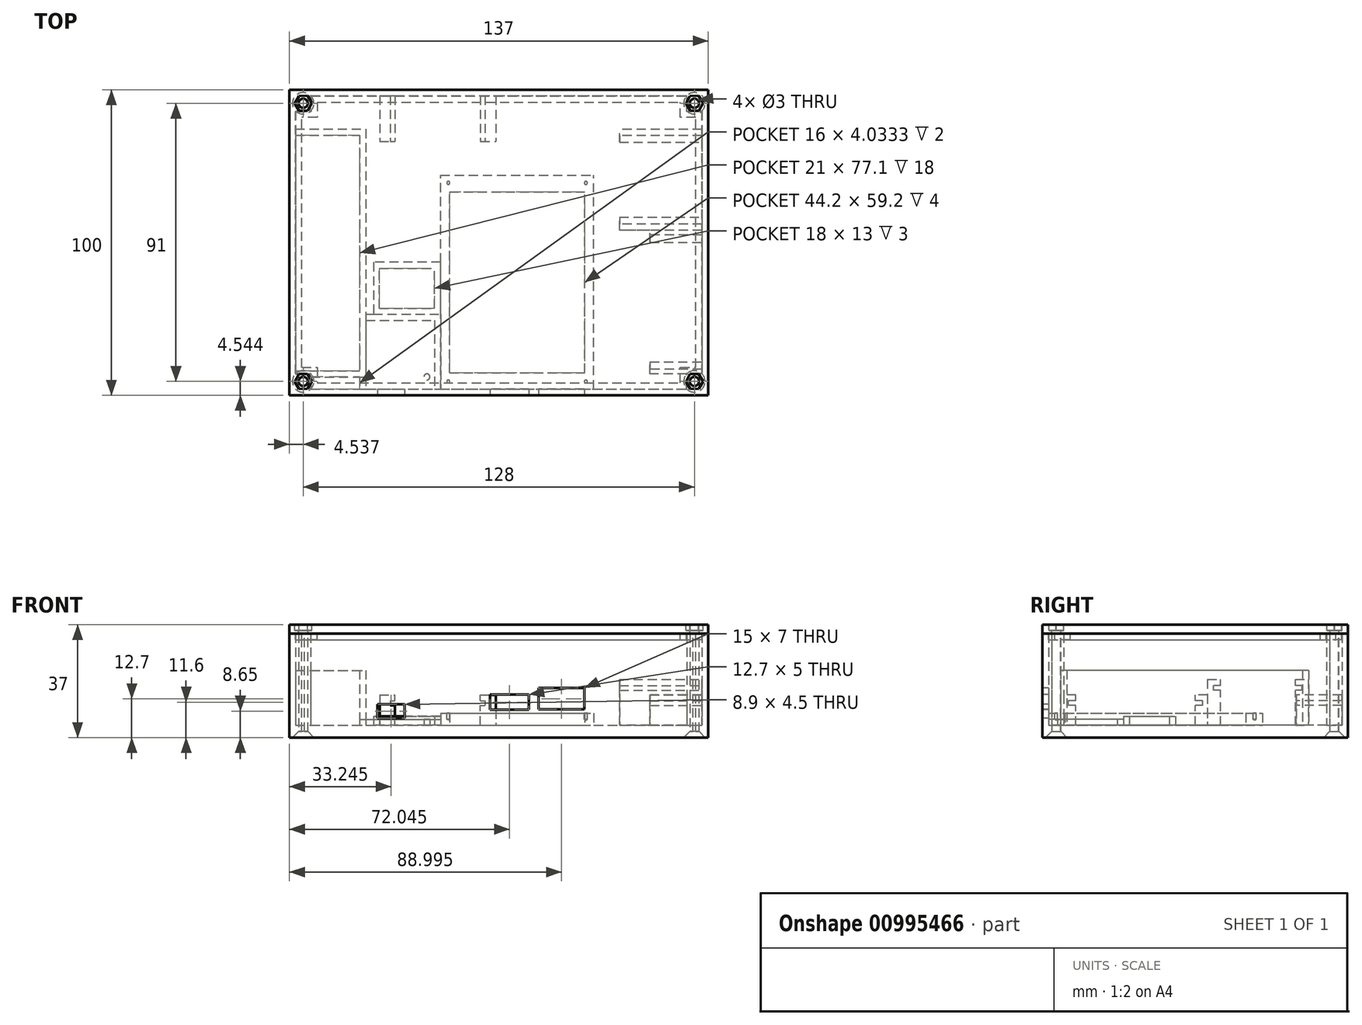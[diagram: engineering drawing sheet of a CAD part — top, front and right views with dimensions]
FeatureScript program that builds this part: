
annotation { "Feature Type Name" : "Feature", "Feature Type Description" : "" }
export const myFeature = defineFeature(function(context is Context, id is Id, definition is map)
    precondition{}
    {
        {
            var Q0;
            Q0=qCreatedBy(makeId("Top.planeOp"),FACE);
            var sketch = newSketch(context, id + "F0", { "sketchPlane" : qUnion([Q0])});
            skLineSegment(sketch, "E0.bottom", {"start": v(-82.47, 29.01) * mm, "end": v(54.53, 29.01) * mm});
            skLineSegment(sketch, "E0.top", {"start": v(-82.47, -70.99) * mm, "end": v(54.53, -70.99) * mm});
            skLineSegment(sketch, "E0.left", {"start": v(-82.47, 29.01) * mm, "end": v(-82.47, -70.99) * mm});
            skLineSegment(sketch, "E0.right", {"start": v(54.53, 29.01) * mm, "end": v(54.53, -70.99) * mm});
            skSolve(sketch);
        }
        {
            var Q0;
            Q0=makeQuery(id+"F0.imprint","IMPRINT",FACE,{"disambiguationData":[TD([[makeQuery(id+"F0.imprint","IMPRINT",EDGE,{"derivedFrom":sQuery(id+"F0.wireOp",EDGE,"E0.bottom")}),-1.0]])]});
            extrude(context, id + "F1", {"entities" : qUnion([Q0]), "oppositeDirection" : true, "depth" : 4 * mm, "offsetDistance" : 25 * mm});
        }
        {
            var Q0;
            Q0=makeQuery(id+"F1.opExtrude","CAP_FACE",FACE,{"disambiguationData":[OSD([sQuery(id+"F0.wireOp",EDGE,"E0.bottom"),sQuery(id+"F0.wireOp",EDGE,"E0.top"),sQuery(id+"F0.wireOp",EDGE,"E0.left"),sQuery(id+"F0.wireOp",EDGE,"E0.right")])],"isStart":true});
            var sketch = newSketch(context, id + "F2", { "sketchPlane" : qUnion([Q0])});
            skLineSegment(sketch, "E1.bottom", {"start": v(-80.47, 27.01) * mm, "end": v(52.53, 27.01) * mm});
            skLineSegment(sketch, "E1.top", {"start": v(-80.47, -68.99) * mm, "end": v(52.53, -68.99) * mm});
            skLineSegment(sketch, "E1.left", {"start": v(-80.47, 27.01) * mm, "end": v(-80.47, -68.99) * mm});
            skLineSegment(sketch, "E1.right", {"start": v(52.53, 27.01) * mm, "end": v(52.53, -68.99) * mm});
            skSolve(sketch);
        }
        {
            var Q0;
            Q0=makeQuery(id+"F2.imprint","IMPRINT",FACE,{"disambiguationData":[TD([[makeQuery(id+"F2.imprint","IMPRINT",EDGE,{"derivedFrom":sQuery(id+"F2.wireOp",EDGE,"E1.bottom")}),1.0]])]});
            extrude(context, id + "F3", {"entities" : qUnion([Q0]), "operationType" : NewBodyOperationType.ADD, "depth" : 30 * mm, "offsetDistance" : 25 * mm});
        }
        {
            var Q0;
            Q0=makeQuery(id+"F1.opExtrude","CAP_FACE",FACE,{"disambiguationData":[OSD([sQuery(id+"F0.wireOp",EDGE,"E0.bottom"),sQuery(id+"F0.wireOp",EDGE,"E0.top"),sQuery(id+"F0.wireOp",EDGE,"E0.left"),sQuery(id+"F0.wireOp",EDGE,"E0.right")])],"isStart":true});
            var sketch = newSketch(context, id + "F4", { "sketchPlane" : qUnion([Q0])});
            skLineSegment(sketch, "E2.bottom", {"start": v(-80.47, 22.01) * mm, "end": v(-75.47, 22.01) * mm});
            skLineSegment(sketch, "E2.top", {"start": v(-80.47, 27.01) * mm, "end": v(-75.47, 27.01) * mm});
            skLineSegment(sketch, "E2.left", {"start": v(-80.47, 22.01) * mm, "end": v(-80.47, 27.01) * mm});
            skLineSegment(sketch, "E2.right", {"start": v(-75.47, 22.01) * mm, "end": v(-75.47, 27.01) * mm});
            skLineSegment(sketch, "E3.0.1.0", {"start": v(-80.47, -68.99) * mm, "end": v(-75.47, -68.99) * mm});
            skLineSegment(sketch, "E3.0.1.1", {"start": v(-75.47, -68.99) * mm, "end": v(-75.47, -63.99) * mm});
            skLineSegment(sketch, "E3.0.1.2", {"start": v(-80.47, -63.99) * mm, "end": v(-75.47, -63.99) * mm});
            skLineSegment(sketch, "E3.0.1.3", {"start": v(-80.47, -68.99) * mm, "end": v(-80.47, -63.99) * mm});
            skLineSegment(sketch, "E3.1.0.0", {"start": v(47.53, 22.01) * mm, "end": v(52.53, 22.01) * mm});
            skLineSegment(sketch, "E3.1.0.1", {"start": v(52.53, 22.01) * mm, "end": v(52.53, 27.01) * mm});
            skLineSegment(sketch, "E3.1.0.2", {"start": v(47.53, 27.01) * mm, "end": v(52.53, 27.01) * mm});
            skLineSegment(sketch, "E3.1.0.3", {"start": v(47.53, 22.01) * mm, "end": v(47.53, 27.01) * mm});
            skLineSegment(sketch, "E3.1.1.0", {"start": v(47.53, -68.99) * mm, "end": v(52.53, -68.99) * mm});
            skLineSegment(sketch, "E3.1.1.1", {"start": v(52.53, -68.99) * mm, "end": v(52.53, -63.99) * mm});
            skLineSegment(sketch, "E3.1.1.2", {"start": v(47.53, -63.99) * mm, "end": v(52.53, -63.99) * mm});
            skLineSegment(sketch, "E3.1.1.3", {"start": v(47.53, -68.99) * mm, "end": v(47.53, -63.99) * mm});
            skLineSegment(sketch, "E3.direction1", {"start": v(-80.47, 22.01) * mm, "end": v(47.53, 22.01) * mm, "construction": true});
            skLineSegment(sketch, "E3.direction2", {"start": v(-80.47, 22.01) * mm, "end": v(-80.47, -68.99) * mm, "construction": true});
            skSolve(sketch);
        }
        {
            var Q0;
            Q0=makeQuery(id+"F4.imprint","IMPRINT",FACE,{"disambiguationData":[TD([[makeQuery(id+"F4.imprint","IMPRINT",EDGE,{"derivedFrom":sQuery(id+"F4.wireOp",EDGE,"E2.bottom")}),1.0]])]});
            var Q1;
            Q1=makeQuery(id+"F4.imprint","IMPRINT",FACE,{"disambiguationData":[TD([[makeQuery(id+"F4.imprint","IMPRINT",EDGE,{"derivedFrom":sQuery(id+"F4.wireOp",EDGE,"E3.1.0.0")}),1.0]])]});
            var Q2;
            Q2=makeQuery(id+"F4.imprint","IMPRINT",FACE,{"disambiguationData":[TD([[makeQuery(id+"F4.imprint","IMPRINT",EDGE,{"derivedFrom":sQuery(id+"F4.wireOp",EDGE,"E3.1.1.0")}),1.0]])]});
            var Q3;
            Q3=makeQuery(id+"F4.imprint","IMPRINT",FACE,{"disambiguationData":[TD([[makeQuery(id+"F4.imprint","IMPRINT",EDGE,{"derivedFrom":sQuery(id+"F4.wireOp",EDGE,"E3.0.1.0")}),1.0]])]});
            extrude(context, id + "F5", {"entities" : qUnion([Q0, Q1, Q2, Q3]), "operationType" : NewBodyOperationType.ADD, "depth" : 30 * mm, "offsetDistance" : 25 * mm});
        }
        {
            var Q0;
            Q0=makeQuery(id+"F1.opExtrude","CAP_FACE",FACE,{"disambiguationData":[OSD([sQuery(id+"F0.wireOp",EDGE,"E0.bottom"),sQuery(id+"F0.wireOp",EDGE,"E0.top"),sQuery(id+"F0.wireOp",EDGE,"E0.left"),sQuery(id+"F0.wireOp",EDGE,"E0.right")])],"isStart":false});
            var sketch = newSketch(context, id + "F6", { "sketchPlane" : qUnion([Q0])});
            skCircle(sketch, "E4", {"center": v(-77.96, 66.46) * mm, "radius": 1.5 * mm});
            skCircle(sketch, "E5.0.1.0", {"center": v(-77.96, -24.54) * mm, "radius": 1.5 * mm});
            skCircle(sketch, "E5.1.0.0", {"center": v(50.04, 66.46) * mm, "radius": 1.5 * mm});
            skCircle(sketch, "E5.1.1.0", {"center": v(50.04, -24.54) * mm, "radius": 1.5 * mm});
            skLineSegment(sketch, "E5.direction1", {"start": v(-77.96, 66.46) * mm, "end": v(50.04, 66.46) * mm, "construction": true});
            skLineSegment(sketch, "E5.direction2", {"start": v(-77.96, 66.46) * mm, "end": v(-77.96, -24.54) * mm, "construction": true});
            skSolve(sketch);
        }
        {
            var Q0;
            Q0=sQuery(id+"F6.wireOp",VERTEX,"E5.direction1.start");
            var Q1;
            Q1=sQuery(id+"F6.wireOp",VERTEX,"E5.direction1.end");
            var Q2;
            Q2=sQuery(id+"F6.wireOp",VERTEX,"E5.1.1.0.center");
            var Q3;
            Q3=sQuery(id+"F6.wireOp",VERTEX,"E5.direction2.end");
            var Q4;
            Q4=makeQuery(id+"F1.opExtrude","SWEPT_BODY",BODY,{"disambiguationData":[OSD([sQuery(id+"F0.wireOp",EDGE,"E0.bottom"),sQuery(id+"F0.wireOp",EDGE,"E0.top"),sQuery(id+"F0.wireOp",EDGE,"E0.left"),sQuery(id+"F0.wireOp",EDGE,"E0.right")])]});
            hole(context, id + "F7", {"style" : HoleStyle.C_SINK, "endStyle" : HoleEndStyle.THROUGH, "holeDiameter" : 3 * mm, "cSinkDiameter" : 7 * mm, "cSinkAngle" : 90 * degree, "majorDiameter" : 5 * mm, "isTappedThrough" : true, "tappedDepth" : 12 * mm, "tapClearance" : 3, "startFromSketch" : true, "locations" : qUnion([Q0, Q1, Q2, Q3]), "scope" : qUnion([Q4])});
        }
        {
            var Q0;
            Q0=makeQuery(id+"F1.opExtrude","CAP_FACE",FACE,{"disambiguationData":[OSD([sQuery(id+"F0.wireOp",EDGE,"E0.bottom"),sQuery(id+"F0.wireOp",EDGE,"E0.top"),sQuery(id+"F0.wireOp",EDGE,"E0.left"),sQuery(id+"F0.wireOp",EDGE,"E0.right")])],"isStart":true});
            var sketch = newSketch(context, id + "F8", { "sketchPlane" : qUnion([Q0])});
            skLineSegment(sketch, "E6.bottom", {"start": v(-80.47, 16.14) * mm, "end": v(-57.47, 16.14) * mm});
            skLineSegment(sketch, "E6.top", {"start": v(-80.47, -64.96) * mm, "end": v(-57.47, -64.96) * mm});
            skLineSegment(sketch, "E6.left", {"start": v(-80.47, 16.14) * mm, "end": v(-80.47, -64.96) * mm});
            skLineSegment(sketch, "E6.right", {"start": v(-57.47, 16.14) * mm, "end": v(-57.47, -64.96) * mm});
            skLineSegment(sketch, "E7.bottom", {"start": v(-80.47, 14.14) * mm, "end": v(-59.47, 14.14) * mm});
            skLineSegment(sketch, "E7.top", {"start": v(-80.47, -62.96) * mm, "end": v(-59.47, -62.96) * mm});
            skLineSegment(sketch, "E7.left", {"start": v(-80.47, 14.14) * mm, "end": v(-80.47, -62.96) * mm});
            skLineSegment(sketch, "E7.right", {"start": v(-59.47, 14.14) * mm, "end": v(-59.47, -62.96) * mm});
            skSolve(sketch);
        }
        {
            var Q0;
            {var subQ1=sQuery(id+"F8.wireOp",EDGE,"E6.bottom");Q0=makeQuery(id+"F8.imprint","IMPRINT",FACE,{"disambiguationData":[TD([[makeQuery(id+"F8.imprint","IMPRINT",EDGE,{"derivedFrom":subQ1}),-1.0]])]});}
            extrude(context, id + "F9", {"entities" : qUnion([Q0]), "operationType" : NewBodyOperationType.ADD, "depth" : 18 * mm, "offsetDistance" : 25 * mm});
        }
        {
            var Q0;
            Q0=makeQuery(id+"F9.boolean.opBoolean","SPLIT",FACE,{"disambiguationData":[TD([makeQuery(id+"F3.opExtrude","SWEPT_FACE",FACE,{"disambiguationData":[OSD([sQuery(id+"F2.wireOp",EDGE,"E1.bottom")])]})])],"derivedFrom":makeQuery(id+"F1.opExtrude","CAP_FACE",FACE,{"disambiguationData":[OSD([sQuery(id+"F0.wireOp",EDGE,"E0.bottom"),sQuery(id+"F0.wireOp",EDGE,"E0.top"),sQuery(id+"F0.wireOp",EDGE,"E0.left"),sQuery(id+"F0.wireOp",EDGE,"E0.right")])],"isStart":true})});
            var sketch = newSketch(context, id + "F10", { "sketchPlane" : qUnion([Q0])});
            skLineSegment(sketch, "E8.bottom", {"start": v(-57.47, -46.49) * mm, "end": v(-34.97, -46.49) * mm});
            skLineSegment(sketch, "E8.top", {"start": v(-57.47, -68.99) * mm, "end": v(-34.97, -68.99) * mm});
            skLineSegment(sketch, "E8.left", {"start": v(-57.47, -46.49) * mm, "end": v(-57.47, -68.99) * mm});
            skLineSegment(sketch, "E8.right", {"start": v(-34.97, -46.49) * mm, "end": v(-34.97, -68.99) * mm});
            skLineSegment(sketch, "E9.bottom", {"start": v(-59.47, -44.49) * mm, "end": v(-32.97, -44.49) * mm});
            skLineSegment(sketch, "E9.top", {"start": v(-59.47, -70.99) * mm, "end": v(-32.97, -70.99) * mm});
            skLineSegment(sketch, "E9.left", {"start": v(-59.47, -44.49) * mm, "end": v(-59.47, -70.99) * mm});
            skLineSegment(sketch, "E9.right", {"start": v(-32.97, -44.49) * mm, "end": v(-32.97, -70.99) * mm});
            skCircle(sketch, "E10", {"center": v(-37.47, -64.99) * mm, "radius": 1 * mm});
            skSolve(sketch);
        }
        {
            var Q0;
            {var subQ5=sQuery(id+"F10.wireOp",EDGE,"E8.bottom");Q0=makeQuery(id+"F10.imprint","IMPRINT",FACE,{"disambiguationData":[TD([[makeQuery(id+"F10.imprint","IMPRINT",EDGE,{"derivedFrom":subQ5}),1.0]])]});}
            var Q1;
            Q1=makeQuery(id+"F10.imprint","IMPRINT",FACE,{"disambiguationData":[TD([[makeQuery(id+"F10.imprint","IMPRINT",EDGE,{"derivedFrom":sQuery(id+"F10.wireOp",EDGE,"E10")}),1.0]])]});
            var Q2;
            {var subQ1=makeQuery(id+"F9.opExtrude","CAP_EDGE",EDGE,{"disambiguationData":[OSD([sQuery(id+"F8.wireOp",EDGE,"E6.top")])],"isStart":true});var subQ5=sQuery(id+"F10.wireOp",EDGE,"E9.left");var subQ7=makeQuery(id+"F10.imprint","INTERSECT",VERTEX,{"derivedFrom":[subQ1,subQ5]});Q2=makeQuery(id+"F10.imprint","IMPRINT",FACE,{"disambiguationData":[TD([[makeQuery(id+"F10.imprint","IMPRINT",EDGE,{"disambiguationData":[TD([[subQ7,-1.0]])],"derivedFrom":subQ5}),1.0]])]});}
            extrude(context, id + "F11", {"entities" : qUnion([Q0, Q1, Q2]), "operationType" : NewBodyOperationType.ADD, "depth" : 2 * mm, "offsetDistance" : 25 * mm});
        }
        {
            var Q0;
            {var subQ5=makeQuery(id+"F3.opExtrude","SWEPT_FACE",FACE,{"disambiguationData":[OSD([sQuery(id+"F2.wireOp",EDGE,"E1.bottom")])]});Q0=makeQuery(id+"F11.boolean.opBoolean","SPLIT",FACE,{"disambiguationData":[TD([subQ5])],"derivedFrom":makeQuery(id+"F9.boolean.opBoolean","SPLIT",FACE,{"disambiguationData":[TD([subQ5])],"derivedFrom":makeQuery(id+"F1.opExtrude","CAP_FACE",FACE,{"disambiguationData":[OSD([sQuery(id+"F0.wireOp",EDGE,"E0.bottom"),sQuery(id+"F0.wireOp",EDGE,"E0.top"),sQuery(id+"F0.wireOp",EDGE,"E0.left"),sQuery(id+"F0.wireOp",EDGE,"E0.right")])],"isStart":true})})});}
            var sketch = newSketch(context, id + "F12", { "sketchPlane" : qUnion([Q0])});
            skLineSegment(sketch, "E11.bottom", {"start": v(-32.97, -68.99) * mm, "end": v(17.03, -68.99) * mm});
            skLineSegment(sketch, "E11.top", {"start": v(-32.97, 1.01) * mm, "end": v(17.03, 1.01) * mm});
            skLineSegment(sketch, "E11.left", {"start": v(-32.97, -68.99) * mm, "end": v(-32.97, 1.01) * mm});
            skLineSegment(sketch, "E11.right", {"start": v(17.03, -68.99) * mm, "end": v(17.03, 1.01) * mm});
            skLineSegment(sketch, "E12.bottom", {"start": v(-30.07, -63.59) * mm, "end": v(14.13, -63.59) * mm});
            skLineSegment(sketch, "E12.top", {"start": v(-30.07, -4.39) * mm, "end": v(14.13, -4.39) * mm});
            skLineSegment(sketch, "E12.left", {"start": v(-30.07, -63.59) * mm, "end": v(-30.07, -4.39) * mm});
            skLineSegment(sketch, "E12.right", {"start": v(14.13, -63.59) * mm, "end": v(14.13, -4.39) * mm});
            skSolve(sketch);
        }
        {
            var Q0;
            {var subQ2=sQuery(id+"F12.wireOp",EDGE,"E11.bottom");Q0=makeQuery(id+"F12.imprint","IMPRINT",FACE,{"disambiguationData":[TD([[makeQuery(id+"F12.imprint","IMPRINT",EDGE,{"derivedFrom":subQ2}),1.0]])]});}
            extrude(context, id + "F13", {"entities" : qUnion([Q0]), "operationType" : NewBodyOperationType.ADD, "depth" : 4 * mm, "offsetDistance" : 25 * mm});
        }
        {
            var Q0;
            Q0=makeQuery(id+"F13.opExtrude","CAP_FACE",FACE,{"disambiguationData":[OSD([sQuery(id+"F12.wireOp",EDGE,"E11.bottom"),sQuery(id+"F12.wireOp",EDGE,"E11.top"),sQuery(id+"F12.wireOp",EDGE,"E11.left"),sQuery(id+"F12.wireOp",EDGE,"E11.right"),sQuery(id+"F12.wireOp",EDGE,"E12.bottom"),sQuery(id+"F12.wireOp",EDGE,"E12.top"),sQuery(id+"F12.wireOp",EDGE,"E12.left"),sQuery(id+"F12.wireOp",EDGE,"E12.right")])],"isStart":false});
            var sketch = newSketch(context, id + "F14", { "sketchPlane" : qUnion([Q0])});
            skCircle(sketch, "E13", {"center": v(-30.47, -1.49) * mm, "radius": 1 * mm});
            skCircle(sketch, "E14.0.1.0", {"center": v(-30.47, -66.49) * mm, "radius": 1 * mm});
            skCircle(sketch, "E14.1.0.0", {"center": v(14.53, -1.49) * mm, "radius": 1 * mm});
            skCircle(sketch, "E14.1.1.0", {"center": v(14.53, -66.49) * mm, "radius": 1 * mm});
            skLineSegment(sketch, "E14.direction1", {"start": v(-30.47, -1.49) * mm, "end": v(14.53, -1.49) * mm, "construction": true});
            skLineSegment(sketch, "E14.direction2", {"start": v(-30.47, -1.49) * mm, "end": v(-30.47, -66.49) * mm, "construction": true});
            skSolve(sketch);
        }
        {
            var Q0;
            Q0=sQuery(id+"F14.wireOp",VERTEX,"E14.direction1.start");
            var Q1;
            Q1=sQuery(id+"F14.wireOp",VERTEX,"E14.direction1.end");
            var Q2;
            Q2=sQuery(id+"F14.wireOp",VERTEX,"E14.1.1.0.center");
            var Q3;
            Q3=sQuery(id+"F14.wireOp",VERTEX,"E14.direction2.end");
            var Q4;
            Q4=makeQuery(id+"F1.opExtrude","SWEPT_BODY",BODY,{"disambiguationData":[OSD([sQuery(id+"F0.wireOp",EDGE,"E0.bottom"),sQuery(id+"F0.wireOp",EDGE,"E0.top"),sQuery(id+"F0.wireOp",EDGE,"E0.left"),sQuery(id+"F0.wireOp",EDGE,"E0.right")])]});
            hole(context, id + "F15", {"style" : HoleStyle.SIMPLE, "endStyle" : HoleEndStyle.BLIND, "holeDiameter" : 1 * mm, "majorDiameter" : 5 * mm, "holeDepth" : 2 * mm, "isTappedThrough" : true, "tappedDepth" : 12 * mm, "tapClearance" : 3, "startFromSketch" : true, "locations" : qUnion([Q0, Q1, Q2, Q3]), "scope" : qUnion([Q4])});
        }
        {
            var Q0;
            {var subQ5=makeQuery(id+"F3.opExtrude","SWEPT_FACE",FACE,{"disambiguationData":[OSD([sQuery(id+"F2.wireOp",EDGE,"E1.bottom")])]});Q0=makeQuery(id+"F13.boolean.opBoolean","SPLIT",FACE,{"disambiguationData":[TD([subQ5])],"derivedFrom":makeQuery(id+"F11.boolean.opBoolean","SPLIT",FACE,{"disambiguationData":[TD([subQ5])],"derivedFrom":makeQuery(id+"F9.boolean.opBoolean","SPLIT",FACE,{"disambiguationData":[TD([subQ5])],"derivedFrom":makeQuery(id+"F1.opExtrude","CAP_FACE",FACE,{"disambiguationData":[OSD([sQuery(id+"F0.wireOp",EDGE,"E0.bottom"),sQuery(id+"F0.wireOp",EDGE,"E0.top"),sQuery(id+"F0.wireOp",EDGE,"E0.left"),sQuery(id+"F0.wireOp",EDGE,"E0.right")])],"isStart":true})})})});}
            var sketch = newSketch(context, id + "F16", { "sketchPlane" : qUnion([Q0])});
            skLineSegment(sketch, "E15.bottom", {"start": v(-32.97, -27.49) * mm, "end": v(-54.97, -27.49) * mm});
            skLineSegment(sketch, "E15.top", {"start": v(-32.97, -44.49) * mm, "end": v(-54.97, -44.49) * mm});
            skLineSegment(sketch, "E15.left", {"start": v(-32.97, -27.49) * mm, "end": v(-32.97, -44.49) * mm});
            skLineSegment(sketch, "E15.right", {"start": v(-54.97, -27.49) * mm, "end": v(-54.97, -44.49) * mm});
            skLineSegment(sketch, "E16.bottom", {"start": v(-52.97, -42.49) * mm, "end": v(-34.97, -42.49) * mm});
            skLineSegment(sketch, "E16.top", {"start": v(-52.97, -29.49) * mm, "end": v(-34.97, -29.49) * mm});
            skLineSegment(sketch, "E16.left", {"start": v(-52.97, -42.49) * mm, "end": v(-52.97, -29.49) * mm});
            skLineSegment(sketch, "E16.right", {"start": v(-34.97, -42.49) * mm, "end": v(-34.97, -29.49) * mm});
            skSolve(sketch);
        }
        {
            var Q0;
            Q0=makeQuery(id+"F16.imprint","IMPRINT",FACE,{"disambiguationData":[TD([[makeQuery(id+"F16.imprint","IMPRINT",EDGE,{"derivedFrom":sQuery(id+"F16.wireOp",EDGE,"E15.bottom")}),1.0]])]});
            extrude(context, id + "F17", {"entities" : qUnion([Q0]), "operationType" : NewBodyOperationType.ADD, "depth" : 3 * mm, "offsetDistance" : 25 * mm});
        }
        {
            var Q0;
            {var subQ6=makeQuery(id+"F3.opExtrude","SWEPT_FACE",FACE,{"disambiguationData":[OSD([sQuery(id+"F2.wireOp",EDGE,"E1.bottom")])]});Q0=makeQuery(id+"F17.boolean.opBoolean","SPLIT",FACE,{"disambiguationData":[TD([subQ6])],"derivedFrom":makeQuery(id+"F13.boolean.opBoolean","SPLIT",FACE,{"disambiguationData":[TD([subQ6])],"derivedFrom":makeQuery(id+"F11.boolean.opBoolean","SPLIT",FACE,{"disambiguationData":[TD([subQ6])],"derivedFrom":makeQuery(id+"F9.boolean.opBoolean","SPLIT",FACE,{"disambiguationData":[TD([subQ6])],"derivedFrom":makeQuery(id+"F1.opExtrude","CAP_FACE",FACE,{"disambiguationData":[OSD([sQuery(id+"F0.wireOp",EDGE,"E0.bottom"),sQuery(id+"F0.wireOp",EDGE,"E0.top"),sQuery(id+"F0.wireOp",EDGE,"E0.left"),sQuery(id+"F0.wireOp",EDGE,"E0.right")])],"isStart":true})})})})});}
            var sketch = newSketch(context, id + "F18", { "sketchPlane" : qUnion([Q0])});
            skLineSegment(sketch, "E17.bottom", {"start": v(52.53, -63.99) * mm, "end": v(35.53, -63.99) * mm});
            skLineSegment(sketch, "E17.top", {"start": v(52.53, -16.99) * mm, "end": v(35.53, -16.99) * mm});
            skLineSegment(sketch, "E17.left", {"start": v(52.53, -63.99) * mm, "end": v(52.53, -16.99) * mm});
            skLineSegment(sketch, "E17.right", {"start": v(35.53, -63.99) * mm, "end": v(35.53, -16.99) * mm});
            skSolve(sketch);
        }
        {
            var Q0;
            Q0=makeQuery(id+"F18.imprint","IMPRINT",FACE,{"disambiguationData":[TD([[makeQuery(id+"F18.imprint","IMPRINT",EDGE,{"derivedFrom":sQuery(id+"F18.wireOp",EDGE,"E17.top")}),1.0]])]});
            extrude(context, id + "F19", {"entities" : qUnion([Q0]), "operationType" : NewBodyOperationType.ADD, "depth" : 10 * mm, "offsetDistance" : 25 * mm});
        }
        {
            var Q0;
            Q0=makeQuery(id+"F19.opExtrude","CAP_FACE",FACE,{"disambiguationData":[OSD([sQuery(id+"F18.wireOp",EDGE,"E17.bottom"),sQuery(id+"F18.wireOp",EDGE,"E17.top"),sQuery(id+"F18.wireOp",EDGE,"E17.left"),sQuery(id+"F18.wireOp",EDGE,"E17.right")])],"isStart":false});
            var sketch = newSketch(context, id + "F20", { "sketchPlane" : qUnion([Q0])});
            skLineSegment(sketch, "E18.bottom", {"start": v(35.53, -20.94) * mm, "end": v(52.53, -20.94) * mm});
            skLineSegment(sketch, "E18.top", {"start": v(35.53, -60.04) * mm, "end": v(52.53, -60.04) * mm});
            skLineSegment(sketch, "E18.left", {"start": v(35.53, -20.94) * mm, "end": v(35.53, -60.04) * mm});
            skLineSegment(sketch, "E18.right", {"start": v(52.53, -20.94) * mm, "end": v(52.53, -60.04) * mm});
            skSolve(sketch);
        }
        {
            var Q0;
            Q0=makeQuery(id+"F20.imprint","IMPRINT",FACE,{"disambiguationData":[TD([[makeQuery(id+"F20.imprint","IMPRINT",EDGE,{"derivedFrom":sQuery(id+"F20.wireOp",EDGE,"E18.bottom")}),-1.0]])]});
            extrude(context, id + "F21", {"entities" : qUnion([Q0]), "operationType" : NewBodyOperationType.REMOVE, "oppositeDirection" : true, "depth" : 10 * mm, "offsetDistance" : 25 * mm});
        }
        {
            var Q0;
            {var subQ1=sQuery(id+"F18.wireOp",EDGE,"E17.right");var subQ2=sQuery(id+"F18.wireOp",EDGE,"E17.top");Q0=makeQuery(id+"F21.boolean.opBoolean","SPLIT",FACE,{"disambiguationData":[TD([makeQuery(id+"F19.opExtrude","SWEPT_FACE",FACE,{"disambiguationData":[OSD([subQ2])]})])],"derivedFrom":makeQuery(id+"F19.opExtrude","SWEPT_FACE",FACE,{"disambiguationData":[OSD([subQ1])]})});}
            var sketch = newSketch(context, id + "F22", { "sketchPlane" : qUnion([Q0])});
            skPoint(sketch, "E19.firstSnap0", {"position": v(20.94, 5) * mm});
            skLineSegment(sketch, "E19.top", {"start": v(18.49, 6.5) * mm, "end": v(62.49, 6.5) * mm});
            skLineSegment(sketch, "E20.top", {"start": v(18.49, 8) * mm, "end": v(62.49, 8) * mm});
            skLineSegment(sketch, "E20.left", {"start": v(18.49, 6.5) * mm, "end": v(18.49, 8) * mm});
            skLineSegment(sketch, "E20.right", {"start": v(62.49, 6.5) * mm, "end": v(62.49, 8) * mm});
            skSolve(sketch);
        }
        {
            var Q0;
            {var subQ0=sQuery(id+"F22.wireOp",EDGE,"E20.right");Q0=makeQuery(id+"F22.imprint","IMPRINT",FACE,{"disambiguationData":[TD([[makeQuery(id+"F22.imprint","IMPRINT",EDGE,{"derivedFrom":subQ0}),1.0]])]});}
            var Q1;
            {var subQ0=sQuery(id+"F22.wireOp",EDGE,"E20.left");Q1=makeQuery(id+"F22.imprint","IMPRINT",FACE,{"disambiguationData":[TD([[makeQuery(id+"F22.imprint","IMPRINT",EDGE,{"derivedFrom":subQ0}),-1.0]])]});}
            extrude(context, id + "F23", {"entities" : qUnion([Q0, Q1]), "operationType" : NewBodyOperationType.REMOVE, "oppositeDirection" : true, "depth" : 17 * mm, "offsetDistance" : 25 * mm});
        }
        {
            var Q0;
            {var subQ6=makeQuery(id+"F3.opExtrude","SWEPT_FACE",FACE,{"disambiguationData":[OSD([sQuery(id+"F2.wireOp",EDGE,"E1.bottom")])]});Q0=makeQuery(id+"F21.boolean.opBoolean","MERGE",FACE,{"derivedFrom":[makeQuery(id+"F17.boolean.opBoolean","SPLIT",FACE,{"disambiguationData":[TD([subQ6])],"derivedFrom":makeQuery(id+"F13.boolean.opBoolean","SPLIT",FACE,{"disambiguationData":[TD([subQ6])],"derivedFrom":makeQuery(id+"F11.boolean.opBoolean","SPLIT",FACE,{"disambiguationData":[TD([subQ6])],"derivedFrom":makeQuery(id+"F9.boolean.opBoolean","SPLIT",FACE,{"disambiguationData":[TD([subQ6])],"derivedFrom":makeQuery(id+"F1.opExtrude","CAP_FACE",FACE,{"disambiguationData":[OSD([sQuery(id+"F0.wireOp",EDGE,"E0.bottom"),sQuery(id+"F0.wireOp",EDGE,"E0.top"),sQuery(id+"F0.wireOp",EDGE,"E0.left"),sQuery(id+"F0.wireOp",EDGE,"E0.right")])],"isStart":true})})})})})],"fromTools":[makeQuery(id+"F21.opExtrude","CAP_FACE",FACE,{"disambiguationData":[OSD([sQuery(id+"F20.wireOp",EDGE,"E18.bottom"),sQuery(id+"F20.wireOp",EDGE,"E18.top"),sQuery(id+"F20.wireOp",EDGE,"E18.left"),sQuery(id+"F20.wireOp",EDGE,"E18.right")])],"isStart":false})]});}
            var sketch = newSketch(context, id + "F24", { "sketchPlane" : qUnion([Q0])});
            skLineSegment(sketch, "E21.bottom", {"start": v(52.53, -16.99) * mm, "end": v(25.53, -16.99) * mm});
            skLineSegment(sketch, "E21.top", {"start": v(52.53, 16.01) * mm, "end": v(25.53, 16.01) * mm});
            skLineSegment(sketch, "E21.left", {"start": v(52.53, -16.99) * mm, "end": v(52.53, 16.01) * mm});
            skLineSegment(sketch, "E21.right", {"start": v(25.53, -16.99) * mm, "end": v(25.53, 16.01) * mm});
            skSolve(sketch);
        }
        {
            var Q0;
            Q0=makeQuery(id+"F24.imprint","IMPRINT",FACE,{"disambiguationData":[TD([[makeQuery(id+"F24.imprint","IMPRINT",EDGE,{"derivedFrom":sQuery(id+"F24.wireOp",EDGE,"E21.top")}),1.0]])]});
            extrude(context, id + "F25", {"entities" : qUnion([Q0]), "operationType" : NewBodyOperationType.ADD, "depth" : 15 * mm, "offsetDistance" : 25 * mm});
        }
        {
            var Q0;
            Q0=makeQuery(id+"F25.opExtrude","CAP_FACE",FACE,{"disambiguationData":[OSD([sQuery(id+"F24.wireOp",EDGE,"E21.bottom"),sQuery(id+"F24.wireOp",EDGE,"E21.top"),sQuery(id+"F24.wireOp",EDGE,"E21.left"),sQuery(id+"F24.wireOp",EDGE,"E21.right")])],"isStart":false});
            var sketch = newSketch(context, id + "F26", { "sketchPlane" : qUnion([Q0])});
            skLineSegment(sketch, "E22.bottom", {"start": v(25.53, 11.76) * mm, "end": v(52.53, 11.76) * mm});
            skLineSegment(sketch, "E22.top", {"start": v(25.53, -12.74) * mm, "end": v(52.53, -12.74) * mm});
            skLineSegment(sketch, "E22.left", {"start": v(25.53, 11.76) * mm, "end": v(25.53, -12.74) * mm});
            skLineSegment(sketch, "E22.right", {"start": v(52.53, 11.76) * mm, "end": v(52.53, -12.74) * mm});
            skSolve(sketch);
        }
        {
            var Q0;
            Q0=makeQuery(id+"F26.imprint","IMPRINT",FACE,{"disambiguationData":[TD([[makeQuery(id+"F26.imprint","IMPRINT",EDGE,{"derivedFrom":sQuery(id+"F26.wireOp",EDGE,"E22.bottom")}),-1.0]])]});
            extrude(context, id + "F27", {"entities" : qUnion([Q0]), "operationType" : NewBodyOperationType.REMOVE, "oppositeDirection" : true, "depth" : 15 * mm, "offsetDistance" : 25 * mm});
        }
        {
            var Q0;
            {var subQ1=sQuery(id+"F24.wireOp",EDGE,"E21.top");var subQ2=sQuery(id+"F24.wireOp",EDGE,"E21.right");Q0=makeQuery(id+"F27.boolean.opBoolean","SPLIT",FACE,{"disambiguationData":[TD([makeQuery(id+"F25.opExtrude","SWEPT_FACE",FACE,{"disambiguationData":[OSD([subQ1])]})])],"derivedFrom":makeQuery(id+"F25.opExtrude","SWEPT_FACE",FACE,{"disambiguationData":[OSD([subQ2])]})});}
            var sketch = newSketch(context, id + "F28", { "sketchPlane" : qUnion([Q0])});
            skLineSegment(sketch, "E23.bottom", {"start": v(-14.01, 11.5) * mm, "end": v(14.99, 11.5) * mm});
            skLineSegment(sketch, "E23.top", {"start": v(-14.01, 13) * mm, "end": v(14.99, 13) * mm});
            skLineSegment(sketch, "E23.left", {"start": v(-14.01, 11.5) * mm, "end": v(-14.01, 13) * mm});
            skLineSegment(sketch, "E23.right", {"start": v(14.99, 11.5) * mm, "end": v(14.99, 13) * mm});
            skSolve(sketch);
        }
        {
            var Q0;
            {var subQ0=sQuery(id+"F28.wireOp",EDGE,"E23.right");Q0=makeQuery(id+"F28.imprint","IMPRINT",FACE,{"disambiguationData":[TD([[makeQuery(id+"F28.imprint","IMPRINT",EDGE,{"derivedFrom":subQ0}),1.0]])]});}
            var Q1;
            {var subQ0=sQuery(id+"F28.wireOp",EDGE,"E23.left");Q1=makeQuery(id+"F28.imprint","IMPRINT",FACE,{"disambiguationData":[TD([[makeQuery(id+"F28.imprint","IMPRINT",EDGE,{"derivedFrom":subQ0}),-1.0]])]});}
            extrude(context, id + "F29", {"entities" : qUnion([Q0, Q1]), "operationType" : NewBodyOperationType.REMOVE, "oppositeDirection" : true, "depth" : 27 * mm, "offsetDistance" : 25 * mm});
        }
        {
            var Q0;
            {var subQ0=sQuery(id+"F0.wireOp",EDGE,"E0.top");Q0=makeQuery(id+"F3.boolean.opBoolean","MERGE",FACE,{"derivedFrom":[makeQuery(id+"F1.opExtrude","SWEPT_FACE",FACE,{"disambiguationData":[OSD([subQ0])]}),makeQuery(id+"F3.opExtrude","SWEPT_FACE",FACE,{"disambiguationData":[OSD([subQ0])]})]});}
            var sketch = newSketch(context, id + "F30", { "sketchPlane" : qUnion([Q0])});
            skLineSegment(sketch, "E24.bottom", {"start": v(14.03, 12.2) * mm, "end": v(-0.97, 12.2) * mm});
            skLineSegment(sketch, "E24.top", {"start": v(14.03, 5.2) * mm, "end": v(-0.97, 5.2) * mm});
            skLineSegment(sketch, "E24.left", {"start": v(14.03, 12.2) * mm, "end": v(14.03, 5.2) * mm});
            skLineSegment(sketch, "E24.right", {"start": v(-0.97, 12.2) * mm, "end": v(-0.97, 5.2) * mm});
            skLineSegment(sketch, "E25.bottom", {"start": v(-4.07, 10.1) * mm, "end": v(-16.77, 10.1) * mm});
            skLineSegment(sketch, "E25.top", {"start": v(-4.07, 5.1) * mm, "end": v(-16.77, 5.1) * mm});
            skLineSegment(sketch, "E25.left", {"start": v(-4.07, 10.1) * mm, "end": v(-4.07, 5.1) * mm});
            skLineSegment(sketch, "E25.right", {"start": v(-16.77, 10.1) * mm, "end": v(-16.77, 5.1) * mm});
            skLineSegment(sketch, "E26.bottom", {"start": v(-53.67, 6.9) * mm, "end": v(-44.77, 6.9) * mm});
            skLineSegment(sketch, "E26.top", {"start": v(-53.67, 2.4) * mm, "end": v(-44.77, 2.4) * mm});
            skLineSegment(sketch, "E26.left", {"start": v(-53.67, 6.9) * mm, "end": v(-53.67, 2.4) * mm});
            skLineSegment(sketch, "E26.right", {"start": v(-44.77, 6.9) * mm, "end": v(-44.77, 2.4) * mm});
            skSolve(sketch);
        }
        {
            var Q0;
            Q0=makeQuery(id+"F30.imprint","IMPRINT",FACE,{"disambiguationData":[TD([[makeQuery(id+"F30.imprint","IMPRINT",EDGE,{"derivedFrom":sQuery(id+"F30.wireOp",EDGE,"E26.bottom")}),-1.0]])]});
            var Q1;
            Q1=makeQuery(id+"F30.imprint","IMPRINT",FACE,{"disambiguationData":[TD([[makeQuery(id+"F30.imprint","IMPRINT",EDGE,{"derivedFrom":sQuery(id+"F30.wireOp",EDGE,"E25.bottom")}),1.0]])]});
            var Q2;
            Q2=makeQuery(id+"F30.imprint","IMPRINT",FACE,{"disambiguationData":[TD([[makeQuery(id+"F30.imprint","IMPRINT",EDGE,{"derivedFrom":sQuery(id+"F30.wireOp",EDGE,"E24.bottom")}),1.0]])]});
            extrude(context, id + "F31", {"entities" : qUnion([Q0, Q1, Q2]), "operationType" : NewBodyOperationType.REMOVE, "oppositeDirection" : true, "depth" : 2 * mm, "offsetDistance" : 25 * mm});
        }
        {
            var Q0;
            {var subQ6=makeQuery(id+"F3.opExtrude","SWEPT_FACE",FACE,{"disambiguationData":[OSD([sQuery(id+"F2.wireOp",EDGE,"E1.bottom")])]});Q0=makeQuery(id+"F27.boolean.opBoolean","MERGE",FACE,{"derivedFrom":[makeQuery(id+"F21.boolean.opBoolean","MERGE",FACE,{"derivedFrom":[makeQuery(id+"F17.boolean.opBoolean","SPLIT",FACE,{"disambiguationData":[TD([subQ6])],"derivedFrom":makeQuery(id+"F13.boolean.opBoolean","SPLIT",FACE,{"disambiguationData":[TD([subQ6])],"derivedFrom":makeQuery(id+"F11.boolean.opBoolean","SPLIT",FACE,{"disambiguationData":[TD([subQ6])],"derivedFrom":makeQuery(id+"F9.boolean.opBoolean","SPLIT",FACE,{"disambiguationData":[TD([subQ6])],"derivedFrom":makeQuery(id+"F1.opExtrude","CAP_FACE",FACE,{"disambiguationData":[OSD([sQuery(id+"F0.wireOp",EDGE,"E0.bottom"),sQuery(id+"F0.wireOp",EDGE,"E0.top"),sQuery(id+"F0.wireOp",EDGE,"E0.left"),sQuery(id+"F0.wireOp",EDGE,"E0.right")])],"isStart":true})})})})})],"fromTools":[makeQuery(id+"F21.opExtrude","CAP_FACE",FACE,{"disambiguationData":[OSD([sQuery(id+"F20.wireOp",EDGE,"E18.bottom"),sQuery(id+"F20.wireOp",EDGE,"E18.top"),sQuery(id+"F20.wireOp",EDGE,"E18.left"),sQuery(id+"F20.wireOp",EDGE,"E18.right")])],"isStart":false})]})],"fromTools":[makeQuery(id+"F27.opExtrude","CAP_FACE",FACE,{"disambiguationData":[OSD([sQuery(id+"F26.wireOp",EDGE,"E22.bottom"),sQuery(id+"F26.wireOp",EDGE,"E22.top"),sQuery(id+"F26.wireOp",EDGE,"E22.left"),sQuery(id+"F26.wireOp",EDGE,"E22.right")])],"isStart":false})]});}
            var sketch = newSketch(context, id + "F32", { "sketchPlane" : qUnion([Q0])});
            skLineSegment(sketch, "E27.bottom", {"start": v(-52.96, 27.01) * mm, "end": v(-14.96, 27.01) * mm});
            skLineSegment(sketch, "E27.top", {"start": v(-52.96, 12.01) * mm, "end": v(-14.96, 12.01) * mm});
            skLineSegment(sketch, "E27.left", {"start": v(-52.96, 27.01) * mm, "end": v(-52.96, 12.01) * mm});
            skLineSegment(sketch, "E27.right", {"start": v(-14.96, 27.01) * mm, "end": v(-14.96, 12.01) * mm});
            skSolve(sketch);
        }
        {
            var Q0;
            Q0=makeQuery(id+"F32.imprint","IMPRINT",FACE,{"disambiguationData":[TD([[makeQuery(id+"F32.imprint","IMPRINT",EDGE,{"derivedFrom":sQuery(id+"F32.wireOp",EDGE,"E27.bottom")}),-1.0]])]});
            extrude(context, id + "F33", {"entities" : qUnion([Q0]), "operationType" : NewBodyOperationType.ADD, "depth" : 10 * mm, "offsetDistance" : 25 * mm});
        }
        {
            var Q0;
            Q0=makeQuery(id+"F33.opExtrude","CAP_FACE",FACE,{"disambiguationData":[OSD([sQuery(id+"F32.wireOp",EDGE,"E27.bottom"),sQuery(id+"F32.wireOp",EDGE,"E27.top"),sQuery(id+"F32.wireOp",EDGE,"E27.left"),sQuery(id+"F32.wireOp",EDGE,"E27.right")])],"isStart":false});
            var sketch = newSketch(context, id + "F34", { "sketchPlane" : qUnion([Q0])});
            skLineSegment(sketch, "E28.bottom", {"start": v(-47.96, 27.01) * mm, "end": v(-19.96, 27.01) * mm});
            skLineSegment(sketch, "E28.top", {"start": v(-47.96, 12.01) * mm, "end": v(-19.96, 12.01) * mm});
            skLineSegment(sketch, "E28.left", {"start": v(-47.96, 27.01) * mm, "end": v(-47.96, 12.01) * mm});
            skLineSegment(sketch, "E28.right", {"start": v(-19.96, 27.01) * mm, "end": v(-19.96, 12.01) * mm});
            skSolve(sketch);
        }
        {
            var Q0;
            Q0=makeQuery(id+"F34.imprint","IMPRINT",FACE,{"disambiguationData":[TD([[makeQuery(id+"F34.imprint","IMPRINT",EDGE,{"derivedFrom":sQuery(id+"F34.wireOp",EDGE,"E28.bottom")}),-1.0]])]});
            extrude(context, id + "F35", {"entities" : qUnion([Q0]), "operationType" : NewBodyOperationType.REMOVE, "oppositeDirection" : true, "depth" : 10 * mm, "offsetDistance" : 25 * mm});
        }
        {
            var Q0;
            {var subQ1=sQuery(id+"F32.wireOp",EDGE,"E27.left");var subQ2=sQuery(id+"F32.wireOp",EDGE,"E27.top");Q0=makeQuery(id+"F35.boolean.opBoolean","SPLIT",FACE,{"disambiguationData":[TD([makeQuery(id+"F33.opExtrude","SWEPT_FACE",FACE,{"disambiguationData":[OSD([subQ1])]})])],"derivedFrom":makeQuery(id+"F33.opExtrude","SWEPT_FACE",FACE,{"disambiguationData":[OSD([subQ2])]})});}
            var sketch = newSketch(context, id + "F36", { "sketchPlane" : qUnion([Q0])});
            skPoint(sketch, "E29.oppositeSnap0", {"position": v(-47.96, 5) * mm});
            skLineSegment(sketch, "E29.bottom", {"start": v(-49.46, 8) * mm, "end": v(-18.46, 8) * mm});
            skLineSegment(sketch, "E29.left", {"start": v(-49.46, 8) * mm, "end": v(-49.46, 6.5) * mm});
            skLineSegment(sketch, "E30", {"start": v(-18.46, 8) * mm, "end": v(-18.46, 6.5) * mm});
            skLineSegment(sketch, "E31", {"start": v(-49.46, 6.5) * mm, "end": v(-18.46, 6.5) * mm});
            skSolve(sketch);
        }
        {
            var Q0;
            {var subQ0=sQuery(id+"F36.wireOp",EDGE,"E29.left");Q0=makeQuery(id+"F36.imprint","IMPRINT",FACE,{"disambiguationData":[TD([[makeQuery(id+"F36.imprint","IMPRINT",EDGE,{"derivedFrom":subQ0}),1.0]])]});}
            var Q1;
            {var subQ0=sQuery(id+"F36.wireOp",EDGE,"E30");Q1=makeQuery(id+"F36.imprint","IMPRINT",FACE,{"disambiguationData":[TD([[makeQuery(id+"F36.imprint","IMPRINT",EDGE,{"derivedFrom":subQ0}),-1.0]])]});}
            extrude(context, id + "F37", {"entities" : qUnion([Q0, Q1]), "operationType" : NewBodyOperationType.REMOVE, "oppositeDirection" : true, "depth" : 15 * mm, "offsetDistance" : 25 * mm});
        }
        {
            var Q0;
            Q0=makeQuery(id+"F5.boolean.opBoolean","MERGE",FACE,{"derivedFrom":[makeQuery(id+"F3.opExtrude","CAP_FACE",FACE,{"disambiguationData":[OSD([sQuery(id+"F0.wireOp",EDGE,"E0.bottom"),sQuery(id+"F0.wireOp",EDGE,"E0.top"),sQuery(id+"F0.wireOp",EDGE,"E0.left"),sQuery(id+"F0.wireOp",EDGE,"E0.right"),sQuery(id+"F2.wireOp",EDGE,"E1.bottom"),sQuery(id+"F2.wireOp",EDGE,"E1.top"),sQuery(id+"F2.wireOp",EDGE,"E1.left"),sQuery(id+"F2.wireOp",EDGE,"E1.right")])],"isStart":false}),makeQuery(id+"F5.opExtrude","CAP_FACE",FACE,{"disambiguationData":[OSD([sQuery(id+"F4.wireOp",EDGE,"E2.bottom"),sQuery(id+"F4.wireOp",EDGE,"E2.top"),sQuery(id+"F4.wireOp",EDGE,"E2.left"),sQuery(id+"F4.wireOp",EDGE,"E2.right")])],"isStart":false}),makeQuery(id+"F5.opExtrude","CAP_FACE",FACE,{"disambiguationData":[OSD([sQuery(id+"F4.wireOp",EDGE,"E3.0.1.0"),sQuery(id+"F4.wireOp",EDGE,"E3.0.1.1"),sQuery(id+"F4.wireOp",EDGE,"E3.0.1.2"),sQuery(id+"F4.wireOp",EDGE,"E3.0.1.3")])],"isStart":false}),makeQuery(id+"F5.opExtrude","CAP_FACE",FACE,{"disambiguationData":[OSD([sQuery(id+"F4.wireOp",EDGE,"E3.1.0.0"),sQuery(id+"F4.wireOp",EDGE,"E3.1.0.1"),sQuery(id+"F4.wireOp",EDGE,"E3.1.0.2"),sQuery(id+"F4.wireOp",EDGE,"E3.1.0.3")])],"isStart":false}),makeQuery(id+"F5.opExtrude","CAP_FACE",FACE,{"disambiguationData":[OSD([sQuery(id+"F4.wireOp",EDGE,"E3.1.1.0"),sQuery(id+"F4.wireOp",EDGE,"E3.1.1.1"),sQuery(id+"F4.wireOp",EDGE,"E3.1.1.2"),sQuery(id+"F4.wireOp",EDGE,"E3.1.1.3")])],"isStart":false})]});
            var sketch = newSketch(context, id + "F38", { "sketchPlane" : qUnion([Q0])});
            skLineSegment(sketch, "E32.bottom", {"start": v(-82.47, 29.01) * mm, "end": v(54.53, 29.01) * mm});
            skLineSegment(sketch, "E32.top", {"start": v(-82.47, -70.99) * mm, "end": v(54.53, -70.99) * mm});
            skLineSegment(sketch, "E32.left", {"start": v(-82.47, 29.01) * mm, "end": v(-82.47, -70.99) * mm});
            skLineSegment(sketch, "E32.right", {"start": v(54.53, 29.01) * mm, "end": v(54.53, -70.99) * mm});
            skSolve(sketch);
        }
        {
            var Q0;
            Q0 = qSketchRegion(id + "F38", true);
            extrude(context, id + "F39", {"entities" : qUnion([Q0]), "depth" : 3 * mm, "offsetDistance" : 25 * mm});
        }
        {
            var Q0;
            Q0=makeQuery(id+"F39.opExtrude","CAP_FACE",FACE,{"disambiguationData":[OSD([sQuery(id+"F38.wireOp",EDGE,"E32.bottom"),sQuery(id+"F38.wireOp",EDGE,"E32.top"),sQuery(id+"F38.wireOp",EDGE,"E32.left"),sQuery(id+"F38.wireOp",EDGE,"E32.right")])],"isStart":true});
            var sketch = newSketch(context, id + "F40", { "sketchPlane" : qUnion([Q0])});
            skLineSegment(sketch, "E33.bottom", {"start": v(-80.42, 68.94) * mm, "end": v(52.48, 68.94) * mm});
            skLineSegment(sketch, "E33.top", {"start": v(-80.42, -26.96) * mm, "end": v(52.48, -26.96) * mm});
            skLineSegment(sketch, "E33.left", {"start": v(-80.42, 68.94) * mm, "end": v(-80.42, -26.96) * mm});
            skLineSegment(sketch, "E33.right", {"start": v(52.48, 68.94) * mm, "end": v(52.48, -26.96) * mm});
            skLineSegment(sketch, "E34.bottom", {"start": v(-80.42, 68.94) * mm, "end": v(-75.4, 68.94) * mm});
            skLineSegment(sketch, "E34.top", {"start": v(-80.42, 63.89) * mm, "end": v(-75.4, 63.89) * mm});
            skLineSegment(sketch, "E34.left", {"start": v(-80.42, 68.94) * mm, "end": v(-80.42, 63.89) * mm});
            skLineSegment(sketch, "E34.right", {"start": v(-75.4, 68.94) * mm, "end": v(-75.4, 63.89) * mm});
            skLineSegment(sketch, "E35.bottom", {"start": v(52.48, 68.94) * mm, "end": v(47.43, 68.94) * mm});
            skLineSegment(sketch, "E35.top", {"start": v(52.48, 63.89) * mm, "end": v(47.43, 63.89) * mm});
            skLineSegment(sketch, "E35.left", {"start": v(52.48, 68.94) * mm, "end": v(52.48, 63.89) * mm});
            skLineSegment(sketch, "E35.right", {"start": v(47.43, 68.94) * mm, "end": v(47.43, 63.89) * mm});
            skLineSegment(sketch, "E36.bottom", {"start": v(52.48, -26.96) * mm, "end": v(47.43, -26.96) * mm});
            skLineSegment(sketch, "E36.top", {"start": v(52.48, -21.91) * mm, "end": v(47.43, -21.91) * mm});
            skLineSegment(sketch, "E36.left", {"start": v(52.48, -26.96) * mm, "end": v(52.48, -21.91) * mm});
            skLineSegment(sketch, "E36.right", {"start": v(47.43, -26.96) * mm, "end": v(47.43, -21.91) * mm});
            skLineSegment(sketch, "E37.bottom", {"start": v(-80.42, -26.96) * mm, "end": v(-75.37, -26.96) * mm});
            skLineSegment(sketch, "E37.top", {"start": v(-80.42, -21.91) * mm, "end": v(-75.37, -21.91) * mm});
            skLineSegment(sketch, "E37.left", {"start": v(-80.42, -26.96) * mm, "end": v(-80.42, -21.91) * mm});
            skLineSegment(sketch, "E37.right", {"start": v(-75.37, -26.96) * mm, "end": v(-75.37, -21.91) * mm});
            skLineSegment(sketch, "E38.bottom", {"start": v(-78.42, 66.94) * mm, "end": v(50.48, 66.94) * mm});
            skLineSegment(sketch, "E38.top", {"start": v(-78.42, -24.96) * mm, "end": v(50.48, -24.96) * mm});
            skLineSegment(sketch, "E38.left", {"start": v(-78.42, 66.94) * mm, "end": v(-78.42, -24.96) * mm});
            skLineSegment(sketch, "E38.right", {"start": v(50.48, 66.94) * mm, "end": v(50.48, -24.96) * mm});
            skLineSegment(sketch, "E39.bottom", {"start": v(-80.42, 61.89) * mm, "end": v(-73.4, 61.89) * mm});
            skLineSegment(sketch, "E39.top", {"start": v(-80.42, 68.94) * mm, "end": v(-73.4, 68.94) * mm});
            skLineSegment(sketch, "E39.left", {"start": v(-80.42, 61.89) * mm, "end": v(-80.42, 68.94) * mm});
            skLineSegment(sketch, "E39.right", {"start": v(-73.4, 61.89) * mm, "end": v(-73.4, 68.94) * mm});
            skLineSegment(sketch, "E40.bottom", {"start": v(45.43, 68.94) * mm, "end": v(52.48, 68.94) * mm});
            skLineSegment(sketch, "E40.top", {"start": v(45.43, 61.89) * mm, "end": v(52.48, 61.89) * mm});
            skLineSegment(sketch, "E40.left", {"start": v(45.43, 68.94) * mm, "end": v(45.43, 61.89) * mm});
            skLineSegment(sketch, "E40.right", {"start": v(52.48, 68.94) * mm, "end": v(52.48, 61.89) * mm});
            skLineSegment(sketch, "E41.bottom", {"start": v(52.48, -19.91) * mm, "end": v(45.43, -19.91) * mm});
            skLineSegment(sketch, "E41.top", {"start": v(52.48, -26.96) * mm, "end": v(45.43, -26.96) * mm});
            skLineSegment(sketch, "E41.left", {"start": v(52.48, -19.91) * mm, "end": v(52.48, -26.96) * mm});
            skLineSegment(sketch, "E41.right", {"start": v(45.43, -19.91) * mm, "end": v(45.43, -26.96) * mm});
            skLineSegment(sketch, "E42.bottom", {"start": v(-73.37, -26.96) * mm, "end": v(-80.42, -26.96) * mm});
            skLineSegment(sketch, "E42.top", {"start": v(-73.37, -19.91) * mm, "end": v(-80.42, -19.91) * mm});
            skLineSegment(sketch, "E42.left", {"start": v(-73.37, -26.96) * mm, "end": v(-73.37, -19.91) * mm});
            skLineSegment(sketch, "E42.right", {"start": v(-80.42, -26.96) * mm, "end": v(-80.42, -19.91) * mm});
            skSolve(sketch);
        }
        {
            var Q0;
            {var subQ0=sQuery(id+"F40.wireOp",EDGE,"E33.bottom");Q0=makeQuery(id+"F40.imprint","IMPRINT",FACE,{"disambiguationData":[TD([[makeQuery(id+"F40.imprint","IMPRINT",EDGE,{"derivedFrom":subQ0}),-1.0]])]});}
            var Q1;
            {var subQ1=sQuery(id+"F40.wireOp",EDGE,"E34.top");var subQ6=sQuery(id+"F40.wireOp",EDGE,"E34.right");var subQ10=makeQuery(id+"F40.imprint","INTERSECT",VERTEX,{"derivedFrom":[subQ1,subQ6]});Q1=makeQuery(id+"F40.imprint","IMPRINT",FACE,{"disambiguationData":[TD([[makeQuery(id+"F40.imprint","IMPRINT",EDGE,{"disambiguationData":[TD([[subQ10,1.0]])],"derivedFrom":subQ1}),-1.0]])]});}
            var Q2;
            {var subQ0=sQuery(id+"F40.wireOp",EDGE,"E39.top");var subQ1=sQuery(id+"F40.wireOp",EDGE,"E34.right");var subQ2=makeQuery(id+"F40.imprint","INTERSECT",VERTEX,{"derivedFrom":[subQ1,subQ0]});Q2=makeQuery(id+"F40.imprint","IMPRINT",FACE,{"disambiguationData":[TD([[makeQuery(id+"F40.imprint","IMPRINT",EDGE,{"disambiguationData":[TD([[subQ2,-1.0]])],"derivedFrom":subQ1}),1.0]])]});}
            var Q3;
            {var subQ0=sQuery(id+"F40.wireOp",EDGE,"E39.left");var subQ1=sQuery(id+"F40.wireOp",EDGE,"E34.top");var subQ2=makeQuery(id+"F40.imprint","INTERSECT",VERTEX,{"derivedFrom":[subQ1,subQ0]});Q3=makeQuery(id+"F40.imprint","IMPRINT",FACE,{"disambiguationData":[TD([[makeQuery(id+"F40.imprint","IMPRINT",EDGE,{"disambiguationData":[TD([[subQ2,-1.0]])],"derivedFrom":subQ1}),-1.0]])]});}
            var Q4;
            {var subQ0=sQuery(id+"F40.wireOp",EDGE,"E33.left");Q4=makeQuery(id+"F40.imprint","IMPRINT",FACE,{"disambiguationData":[TD([[makeQuery(id+"F40.imprint","IMPRINT",EDGE,{"derivedFrom":subQ0}),1.0]])]});}
            var Q5;
            {var subQ0=sQuery(id+"F40.wireOp",EDGE,"E41.top");var subQ1=sQuery(id+"F40.wireOp",EDGE,"E36.right");var subQ2=makeQuery(id+"F40.imprint","INTERSECT",VERTEX,{"derivedFrom":[subQ1,subQ0]});Q5=makeQuery(id+"F40.imprint","IMPRINT",FACE,{"disambiguationData":[TD([[makeQuery(id+"F40.imprint","IMPRINT",EDGE,{"disambiguationData":[TD([[subQ2,-1.0]])],"derivedFrom":subQ1}),1.0]])]});}
            var Q6;
            {var subQ0=sQuery(id+"F40.wireOp",EDGE,"E41.left");var subQ1=sQuery(id+"F40.wireOp",EDGE,"E36.top");var subQ2=makeQuery(id+"F40.imprint","INTERSECT",VERTEX,{"derivedFrom":[subQ1,subQ0]});Q6=makeQuery(id+"F40.imprint","IMPRINT",FACE,{"disambiguationData":[TD([[makeQuery(id+"F40.imprint","IMPRINT",EDGE,{"disambiguationData":[TD([[subQ2,-1.0]])],"derivedFrom":subQ1}),-1.0]])]});}
            var Q7;
            {var subQ0=sQuery(id+"F40.wireOp",EDGE,"E33.right");Q7=makeQuery(id+"F40.imprint","IMPRINT",FACE,{"disambiguationData":[TD([[makeQuery(id+"F40.imprint","IMPRINT",EDGE,{"derivedFrom":subQ0}),-1.0]])]});}
            var Q8;
            {var subQ1=sQuery(id+"F40.wireOp",EDGE,"E35.right");var subQ6=sQuery(id+"F40.wireOp",EDGE,"E35.top");var subQ10=makeQuery(id+"F40.imprint","INTERSECT",VERTEX,{"derivedFrom":[subQ6,subQ1]});Q8=makeQuery(id+"F40.imprint","IMPRINT",FACE,{"disambiguationData":[TD([[makeQuery(id+"F40.imprint","IMPRINT",EDGE,{"disambiguationData":[TD([[subQ10,1.0]])],"derivedFrom":subQ6}),1.0]])]});}
            var Q9;
            {var subQ0=sQuery(id+"F40.wireOp",EDGE,"E40.bottom");var subQ1=sQuery(id+"F40.wireOp",EDGE,"E35.right");var subQ2=makeQuery(id+"F40.imprint","INTERSECT",VERTEX,{"derivedFrom":[subQ1,subQ0]});Q9=makeQuery(id+"F40.imprint","IMPRINT",FACE,{"disambiguationData":[TD([[makeQuery(id+"F40.imprint","IMPRINT",EDGE,{"disambiguationData":[TD([[subQ2,-1.0]])],"derivedFrom":subQ1}),-1.0]])]});}
            var Q10;
            {var subQ0=sQuery(id+"F40.wireOp",EDGE,"E40.right");var subQ1=sQuery(id+"F40.wireOp",EDGE,"E35.top");var subQ2=makeQuery(id+"F40.imprint","INTERSECT",VERTEX,{"derivedFrom":[subQ1,subQ0]});Q10=makeQuery(id+"F40.imprint","IMPRINT",FACE,{"disambiguationData":[TD([[makeQuery(id+"F40.imprint","IMPRINT",EDGE,{"disambiguationData":[TD([[subQ2,-1.0]])],"derivedFrom":subQ1}),1.0]])]});}
            var Q11;
            {var subQ1=sQuery(id+"F40.wireOp",EDGE,"E37.top");var subQ8=sQuery(id+"F40.wireOp",EDGE,"E37.right");var subQ11=makeQuery(id+"F40.imprint","INTERSECT",VERTEX,{"derivedFrom":[subQ1,subQ8]});Q11=makeQuery(id+"F40.imprint","IMPRINT",FACE,{"disambiguationData":[TD([[makeQuery(id+"F40.imprint","IMPRINT",EDGE,{"disambiguationData":[TD([[subQ11,1.0]])],"derivedFrom":subQ1}),1.0]])]});}
            var Q12;
            {var subQ0=sQuery(id+"F40.wireOp",EDGE,"E36.right");var subQ1=sQuery(id+"F40.wireOp",EDGE,"E36.top");var subQ2=makeQuery(id+"F40.imprint","INTERSECT",VERTEX,{"derivedFrom":[subQ1,subQ0]});Q12=makeQuery(id+"F40.imprint","IMPRINT",FACE,{"disambiguationData":[TD([[makeQuery(id+"F40.imprint","IMPRINT",EDGE,{"disambiguationData":[TD([[subQ2,1.0]])],"derivedFrom":subQ1}),-1.0]])]});}
            var Q13;
            {var subQ0=sQuery(id+"F40.wireOp",EDGE,"E33.top");Q13=makeQuery(id+"F40.imprint","IMPRINT",FACE,{"disambiguationData":[TD([[makeQuery(id+"F40.imprint","IMPRINT",EDGE,{"derivedFrom":subQ0}),1.0]])]});}
            var Q14;
            {var subQ0=sQuery(id+"F40.wireOp",EDGE,"E42.right");var subQ1=sQuery(id+"F40.wireOp",EDGE,"E37.top");var subQ2=makeQuery(id+"F40.imprint","INTERSECT",VERTEX,{"derivedFrom":[subQ1,subQ0]});Q14=makeQuery(id+"F40.imprint","IMPRINT",FACE,{"disambiguationData":[TD([[makeQuery(id+"F40.imprint","IMPRINT",EDGE,{"disambiguationData":[TD([[subQ2,-1.0]])],"derivedFrom":subQ1}),1.0]])]});}
            var Q15;
            {var subQ0=sQuery(id+"F40.wireOp",EDGE,"E42.bottom");var subQ1=sQuery(id+"F40.wireOp",EDGE,"E37.right");var subQ2=makeQuery(id+"F40.imprint","INTERSECT",VERTEX,{"derivedFrom":[subQ1,subQ0]});Q15=makeQuery(id+"F40.imprint","IMPRINT",FACE,{"disambiguationData":[TD([[makeQuery(id+"F40.imprint","IMPRINT",EDGE,{"disambiguationData":[TD([[subQ2,-1.0]])],"derivedFrom":subQ1}),-1.0]])]});}
            extrude(context, id + "F41", {"entities" : qUnion([Q0, Q1, Q2, Q3, Q4, Q5, Q6, Q7, Q8, Q9, Q10, Q11, Q12, Q13, Q14, Q15]), "operationType" : NewBodyOperationType.ADD, "depth" : 2 * mm, "offsetDistance" : 25 * mm});
        }
        {
            var Q0;
            Q0=makeQuery(id+"F39.opExtrude","CAP_FACE",FACE,{"disambiguationData":[OSD([sQuery(id+"F38.wireOp",EDGE,"E32.bottom"),sQuery(id+"F38.wireOp",EDGE,"E32.top"),sQuery(id+"F38.wireOp",EDGE,"E32.left"),sQuery(id+"F38.wireOp",EDGE,"E32.right")])],"isStart":false});
            var sketch = newSketch(context, id + "F42", { "sketchPlane" : qUnion([Q0])});
            skCircle(sketch, "E43", {"center": v(-77.93, 24.55) * mm, "radius": 1.5 * mm});
            skCircle(sketch, "E44.cCircle", {"center": v(-77.93, 24.55) * mm, "radius": 2.43 * mm, "construction": true});
            skLineSegment(sketch, "E44.0", {"start": v(-80.73, 24.5) * mm, "end": v(-79.37, 26.96) * mm});
            skLineSegment(sketch, "E44.1", {"start": v(-79.37, 26.96) * mm, "end": v(-76.57, 27) * mm});
            skLineSegment(sketch, "E44.2", {"start": v(-76.57, 27) * mm, "end": v(-75.13, 24.6) * mm});
            skLineSegment(sketch, "E44.3", {"start": v(-75.13, 24.6) * mm, "end": v(-76.5, 22.15) * mm});
            skLineSegment(sketch, "E44.4", {"start": v(-76.5, 22.15) * mm, "end": v(-79.3, 22.1) * mm});
            skLineSegment(sketch, "E44.5", {"start": v(-79.3, 22.1) * mm, "end": v(-80.73, 24.5) * mm});
            skPoint(sketch, "E44.0.midPoint", {"position": v(-80.05, 25.73) * mm});
            skCircle(sketch, "E45.0.1.0", {"center": v(-77.93, -66.45) * mm, "radius": 2.43 * mm, "construction": true});
            skLineSegment(sketch, "E45.0.1.1", {"start": v(-79.37, -64.04) * mm, "end": v(-76.57, -64) * mm});
            skLineSegment(sketch, "E45.0.1.2", {"start": v(-76.57, -64) * mm, "end": v(-75.13, -66.4) * mm});
            skLineSegment(sketch, "E45.0.1.3", {"start": v(-75.13, -66.4) * mm, "end": v(-76.5, -68.85) * mm});
            skLineSegment(sketch, "E45.0.1.4", {"start": v(-76.5, -68.85) * mm, "end": v(-79.3, -68.9) * mm});
            skLineSegment(sketch, "E45.0.1.5", {"start": v(-79.3, -68.9) * mm, "end": v(-80.73, -66.5) * mm});
            skLineSegment(sketch, "E45.0.1.6", {"start": v(-80.73, -66.5) * mm, "end": v(-79.37, -64.04) * mm});
            skCircle(sketch, "E45.0.1.7", {"center": v(-77.93, -66.45) * mm, "radius": 1.5 * mm});
            skCircle(sketch, "E45.1.0.0", {"center": v(50.07, 24.55) * mm, "radius": 2.43 * mm, "construction": true});
            skLineSegment(sketch, "E45.1.0.1", {"start": v(48.63, 26.96) * mm, "end": v(51.43, 27) * mm});
            skLineSegment(sketch, "E45.1.0.2", {"start": v(51.43, 27) * mm, "end": v(52.87, 24.6) * mm});
            skLineSegment(sketch, "E45.1.0.3", {"start": v(52.87, 24.6) * mm, "end": v(51.5, 22.15) * mm});
            skLineSegment(sketch, "E45.1.0.4", {"start": v(51.5, 22.15) * mm, "end": v(48.7, 22.1) * mm});
            skLineSegment(sketch, "E45.1.0.5", {"start": v(48.7, 22.1) * mm, "end": v(47.27, 24.5) * mm});
            skLineSegment(sketch, "E45.1.0.6", {"start": v(47.27, 24.5) * mm, "end": v(48.63, 26.96) * mm});
            skCircle(sketch, "E45.1.0.7", {"center": v(50.07, 24.55) * mm, "radius": 1.5 * mm});
            skCircle(sketch, "E45.1.1.0", {"center": v(50.07, -66.45) * mm, "radius": 2.43 * mm, "construction": true});
            skLineSegment(sketch, "E45.1.1.1", {"start": v(48.63, -64.04) * mm, "end": v(51.43, -64) * mm});
            skLineSegment(sketch, "E45.1.1.2", {"start": v(51.43, -64) * mm, "end": v(52.87, -66.4) * mm});
            skLineSegment(sketch, "E45.1.1.3", {"start": v(52.87, -66.4) * mm, "end": v(51.5, -68.85) * mm});
            skLineSegment(sketch, "E45.1.1.4", {"start": v(51.5, -68.85) * mm, "end": v(48.7, -68.9) * mm});
            skLineSegment(sketch, "E45.1.1.5", {"start": v(48.7, -68.9) * mm, "end": v(47.27, -66.5) * mm});
            skLineSegment(sketch, "E45.1.1.6", {"start": v(47.27, -66.5) * mm, "end": v(48.63, -64.04) * mm});
            skCircle(sketch, "E45.1.1.7", {"center": v(50.07, -66.45) * mm, "radius": 1.5 * mm});
            skLineSegment(sketch, "E45.direction1", {"start": v(-77.93, 24.55) * mm, "end": v(50.07, 24.55) * mm, "construction": true});
            skLineSegment(sketch, "E45.direction2", {"start": v(-77.93, 24.55) * mm, "end": v(-77.93, -66.45) * mm, "construction": true});
            skSolve(sketch);
        }
        {
            var Q0;
            Q0=sQuery(id+"F42.wireOp",VERTEX,"E45.direction1.start");
            var Q1;
            Q1=sQuery(id+"F42.wireOp",VERTEX,"E45.direction1.end");
            var Q2;
            Q2=sQuery(id+"F42.wireOp",VERTEX,"E45.1.1.0.center");
            var Q3;
            Q3=sQuery(id+"F42.wireOp",VERTEX,"E45.direction2.end");
            var Q4;
            Q4=makeQuery(id+"F1.opExtrude","SWEPT_BODY",BODY,{"disambiguationData":[OSD([sQuery(id+"F0.wireOp",EDGE,"E0.bottom"),sQuery(id+"F0.wireOp",EDGE,"E0.top"),sQuery(id+"F0.wireOp",EDGE,"E0.left"),sQuery(id+"F0.wireOp",EDGE,"E0.right")])]});
            var Q5;
            Q5=makeQuery(id+"F39.opExtrude","SWEPT_BODY",BODY,{"disambiguationData":[OSD([sQuery(id+"F38.wireOp",EDGE,"E32.bottom"),sQuery(id+"F38.wireOp",EDGE,"E32.top"),sQuery(id+"F38.wireOp",EDGE,"E32.left"),sQuery(id+"F38.wireOp",EDGE,"E32.right")])]});
            hole(context, id + "F43", {"style" : HoleStyle.SIMPLE, "endStyle" : HoleEndStyle.THROUGH, "holeDiameter" : 3 * mm, "majorDiameter" : 5 * mm, "isTappedThrough" : true, "tappedDepth" : 12 * mm, "tapClearance" : 3, "startFromSketch" : true, "locations" : qUnion([Q0, Q1, Q2, Q3]), "scope" : qUnion([Q4, Q5])});
        }
        {
            var Q0;
            Q0 = qSketchRegion(id + "F42", true);
            extrude(context, id + "F44", {"entities" : qUnion([Q0]), "operationType" : NewBodyOperationType.REMOVE, "oppositeDirection" : true, "depth" : 2 * mm, "offsetDistance" : 25 * mm});
        }
    });
